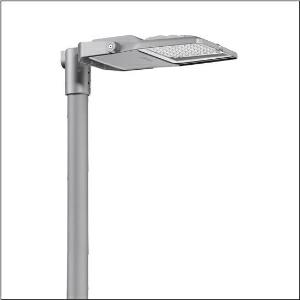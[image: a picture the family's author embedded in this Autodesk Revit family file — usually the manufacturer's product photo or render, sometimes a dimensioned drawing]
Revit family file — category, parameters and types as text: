
# Revit family: floodlight_fl_21_iq_mini___pl61_5xa7772d2c3a_9c70
name_source: partatom
category: Lighting Fixtures
units: mm (PartAtom-declared; Revit-internal decimal feet)

## family parameters
Cut with Voids When Loaded = No
Host = Face
Light Source = No
Part Type = Normal
Room Calculation Point = No
Round Connector Dimension = Use Diameter
Shared = No

## types (1)
- --- (1 x LED, 17500 lm, 143 W, 3000K)
    Apparent Load = 143 VA
    CIE Flux Codes = 33 65 98 100 100
    Color Rendering = 70
    Color Temperature = 3000K
    Default Elevation = 1800 mm
    Description = Floodlight FL 21 iQ mini, floodlight, primary light control with lens, of PMMA, primary optical cover: protective disc, of toughened safety glass, transparent, light distribution: PL61, light emission: direct distribution, installation type: surface-mounted, LED, High Power LED, rated luminous flux: 17.500lm, luminous efficacy: 122lm/W, light colour: 730, colour temperature: 3000K, control: Auto-Match, Temp-Guard, Night-Set, Smart-Wire, Desk-Remote (wireless, voltage-free reading and setting of iQ features in the workshop via application-optimized NFC function/RFID function), optimised constant luminous flux control (CLO 2.0), Light-Fading, Lumen-Switch, with terminal, 6-pole, mains connection: 220..240V, AC, 50/60Hz, start of lifetime: 143W, end of service life: 152W, reduction: 61W, luminaire housing, of diecast aluminium, powder-coated, Siteco® metallic grey (DB 702S), corrosivity category C5 mid according to DIN EN ISO 12944, sealing non-destructively replaceable, please order mast flange separately, mast bracket, of steel, galvanised, powder-coated, protection rating (complete): IP66, insulation class (complete): insulation class II (safety insulation), certification: CE, ENEC, VDE, protection symbol: D, impact resistance: IK08, permissible operating ambient temperature: -40..+40°C, permissible operating ambient temperature for outdoor applications: -40..+50°C, standard: DIN EN 12944, LABS conformity tested according to VDMA 24364:2018-05, packaging unit: 1 piece

Light Distribution: PL61
    Height = 70 mm
    Lamp = 1 x LED
    Lamp Light Flux = 17500 lm
    Lamp Power = 143 W
    Lamp count = 1
    Length = 485 mm
    Luminous efficacy = 122 lm/W
    Manufacturer = Siteco
    ModVariant = No
    Model = 5XA7772D2C3A
    Number of Poles = 1
    OnlyDefault = Yes
    Power Factor = 1
    Product Name = Floodlight FL 21 iQ mini | PL61
    Product group = floodlight | pylon annexe
    ProductGroupID = 6200
    Protection Class = Protection class II
    Protection Degree = IP 66
    RLX_Detail_Level = 1
    RLX_Emergency_Light_Flux = 0 lm
    RLX_Emergency_Type = 0
    RLX_Emergency_Type_DB = No
    RlxData = <blob elided: 101565 chars, md5=d25d6627>
    Socket = socket
    Standby Power = 0 W
    System Light Flux = 17500 lm
    System Power = 143 W
    Type Comments = factory setting: luminous flux: 100 % | dim-lin: 254 | 730 mA
    Type Image = l_1007125.jpg
    URL = http://relux.com
    VarID = @adj_105527
    Voltage = 0 V
    Weight = 0.00 kg
    Width = 337 mm

## geometry (parser evidence)
native form markers: Blend x4, Sweep x11
no freeform markers — native parametric forms only
